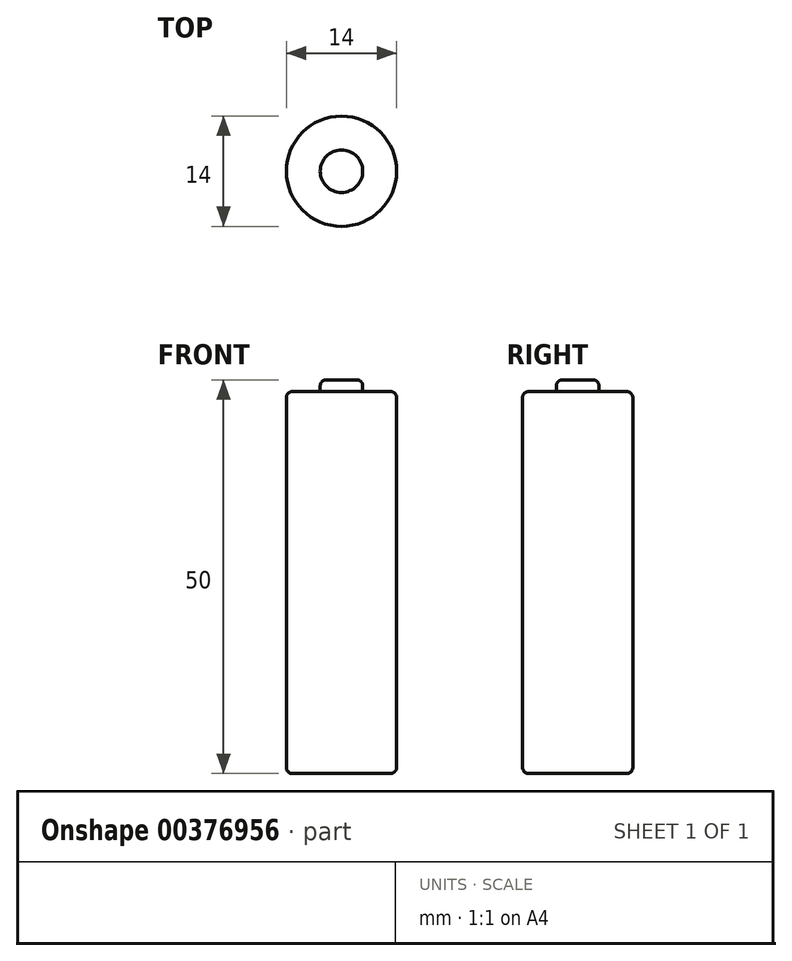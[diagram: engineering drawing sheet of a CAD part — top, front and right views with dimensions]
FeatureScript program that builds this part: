
annotation { "Feature Type Name" : "Feature", "Feature Type Description" : "" }
export const myFeature = defineFeature(function(context is Context, id is Id, definition is map)
    precondition{}
    {
        {
            var Q0;
            Q0=qCreatedBy(makeId("Top.planeOp"),FACE);
            var sketch = newSketch(context, id + "F0", { "sketchPlane" : qUnion([Q0])});
            skCircle(sketch, "E0", {"center": v(0, 0) * mm, "radius": 7 * mm});
            skSolve(sketch);
        }
        {
            var Q0;
            Q0=makeQuery(id+"F0.imprint","IMPRINT",FACE,{"disambiguationData":[TD([[makeQuery(id+"F0.imprint","IMPRINT",EDGE,{"derivedFrom":sQuery(id+"F0.wireOp",EDGE,"E0")}),1.0]])]});
            extrude(context, id + "F1", {"entities" : qUnion([Q0]), "depth" : 48.5 * mm});
        }
        {
            var Q0;
            Q0=makeQuery(id+"F1.opExtrude","CAP_FACE",FACE,{"disambiguationData":[OSD([sQuery(id+"F0.wireOp",EDGE,"E0")])],"isStart":false});
            var sketch = newSketch(context, id + "F2", { "sketchPlane" : qUnion([Q0])});
            skCircle(sketch, "E1", {"center": v(0, 0) * mm, "radius": 2.7 * mm});
            skSolve(sketch);
        }
        {
            var Q0;
            Q0=makeQuery(id+"F2.imprint","IMPRINT",FACE,{"disambiguationData":[TD([[makeQuery(id+"F2.imprint","IMPRINT",EDGE,{"derivedFrom":sQuery(id+"F2.wireOp",EDGE,"E1")}),1.0]])]});
            extrude(context, id + "F3", {"entities" : qUnion([Q0]), "operationType" : NewBodyOperationType.ADD, "depth" : 1.5 * mm});
        }
        {
            var Q0;
            Q0=makeQuery(id+"F3.opExtrude","CAP_EDGE",EDGE,{"disambiguationData":[OSD([sQuery(id+"F2.wireOp",EDGE,"E1")])],"isStart":false});
            var Q1;
            Q1=makeQuery(id+"F1.opExtrude","CAP_EDGE",EDGE,{"disambiguationData":[OSD([sQuery(id+"F0.wireOp",EDGE,"E0")])],"isStart":false});
            var Q2;
            Q2=makeQuery(id+"F1.opExtrude","CAP_EDGE",EDGE,{"disambiguationData":[OSD([sQuery(id+"F0.wireOp",EDGE,"E0")])],"isStart":true});
            fillet(context, id + "F4", {"entities" : qUnion([Q0, Q1, Q2]), "radius" : 0.75 * mm, "tangentPropagation" : true, "allowEdgeOverflow" : false});
        }
    });
